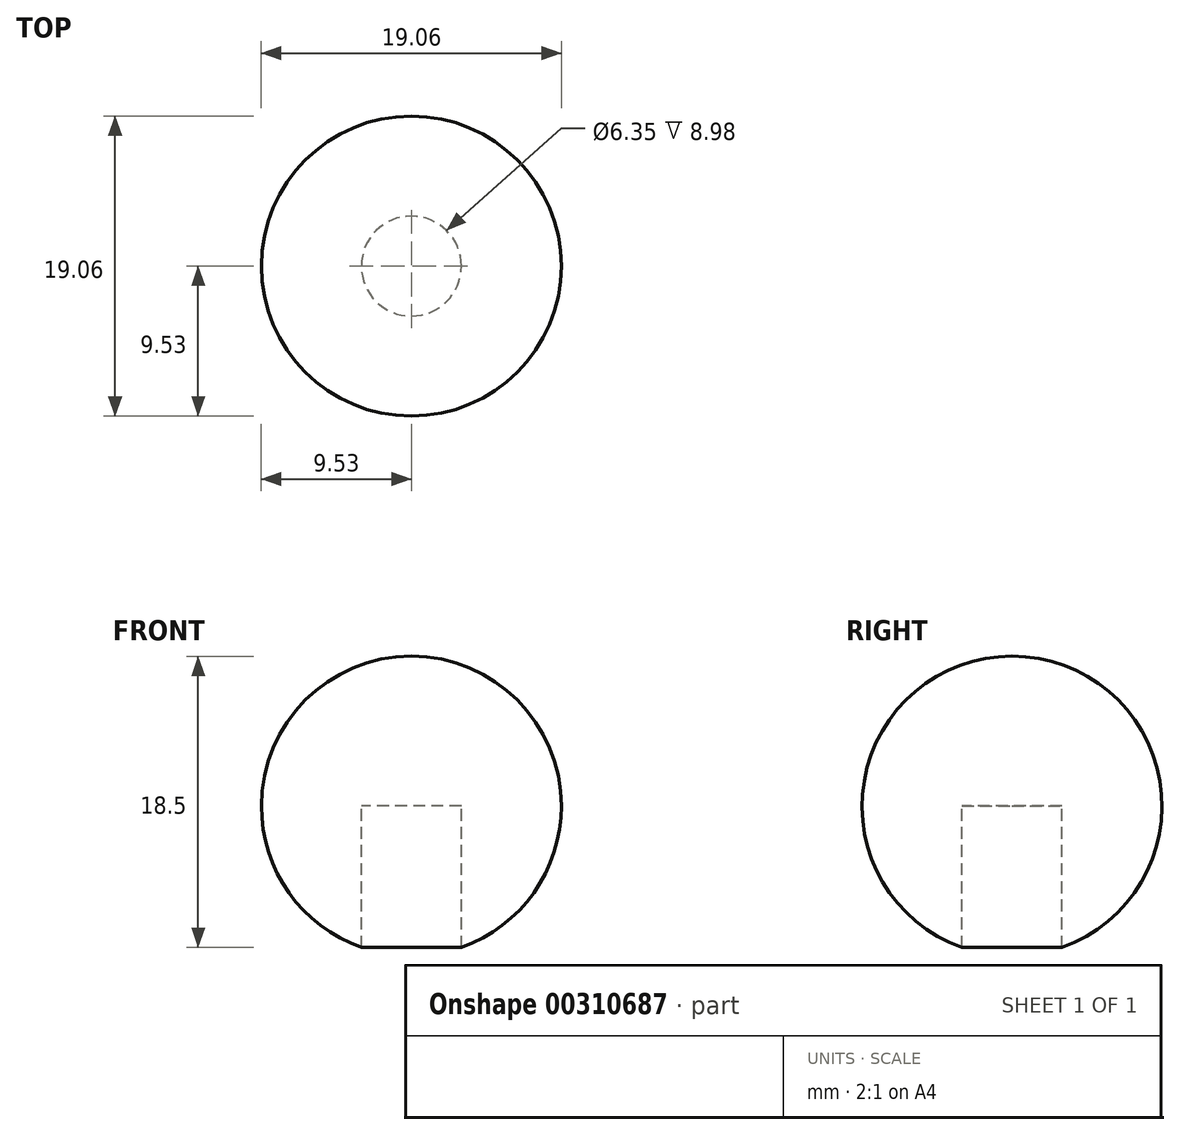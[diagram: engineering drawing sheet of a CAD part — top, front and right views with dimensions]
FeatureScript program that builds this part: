
annotation { "Feature Type Name" : "Feature", "Feature Type Description" : "" }
export const myFeature = defineFeature(function(context is Context, id is Id, definition is map)
    precondition{}
    {
        {
            var Q0;
            Q0=qCreatedBy(makeId("Front.planeOp"),FACE);
            var sketch = newSketch(context, id + "F0", { "sketchPlane" : qUnion([Q0])});
            skArc(sketch, "E0", {"start": v(-9.52, 0) * mm, "mid": v(0, -9.52) * mm, "end": v(9.52, 0) * mm});
            skLineSegment(sketch, "E1", {"start": v(9.52, 0) * mm, "end": v(-9.52, 0) * mm});
            skSolve(sketch);
        }
        {
            var Q0;
            Q0=qCreatedBy(makeId("Right.planeOp"),FACE);
            var sketch = newSketch(context, id + "F1", { "sketchPlane" : qUnion([Q0])});
            skCircle(sketch, "E2", {"center": v(0, 0) * mm, "radius": 9.52 * mm});
            skSolve(sketch);
        }
        {
            var Q0;
            Q0 = qSketchRegion(id + "F0", true);
            var Q1;
            Q1=sQuery(id+"F1.wireOp",EDGE,"E2");
            revolve(context, id + "F2", {"entities" : qUnion([Q0]), "axis" : qUnion([Q1]), "revolveType" : RevolveType.FULL});
        }
        {
            var Q0;
            Q0=qCreatedBy(makeId("Top.planeOp"),FACE);
            var sketch = newSketch(context, id + "F3", { "sketchPlane" : qUnion([Q0])});
            skCircle(sketch, "E3", {"center": v(0, 0) * mm, "radius": 3.18 * mm});
            skSolve(sketch);
        }
        {
            var Q0;
            Q0 = qSketchRegion(id + "F3", true);
            extrude(context, id + "F4", {"entities" : qUnion([Q0]), "operationType" : NewBodyOperationType.REMOVE, "oppositeDirection" : true, "depth" : 25.4 * mm});
        }
    });
